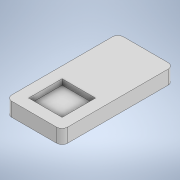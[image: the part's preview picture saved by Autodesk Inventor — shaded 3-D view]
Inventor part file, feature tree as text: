
AUTODESK INVENTOR PART (.ipt)
format: ipt  version: 2021 (Build 250183000, 183)  size: 119,296 bytes
history: native  units: mm
features: extrude x2, sketch x2, other x1, fillet x1, mirror x1
ambient origin geometry x8: Origin, YZ Plane, XZ Plane, XY Plane, X Axis, Y Axis, Z Axis, Center Point
bodies: Body1 (feature_tree)
feature tree (7):
  other  "實體1"
  extrude  "擠出1"  Depth=20.0mm
  extrude  "擠出2"  Depth=40.0mm
  fillet  "圓角1"  Radius=5.0mm
  mirror  "鏡射1"
  sketch  "草圖1"
  sketch  "草圖2"
